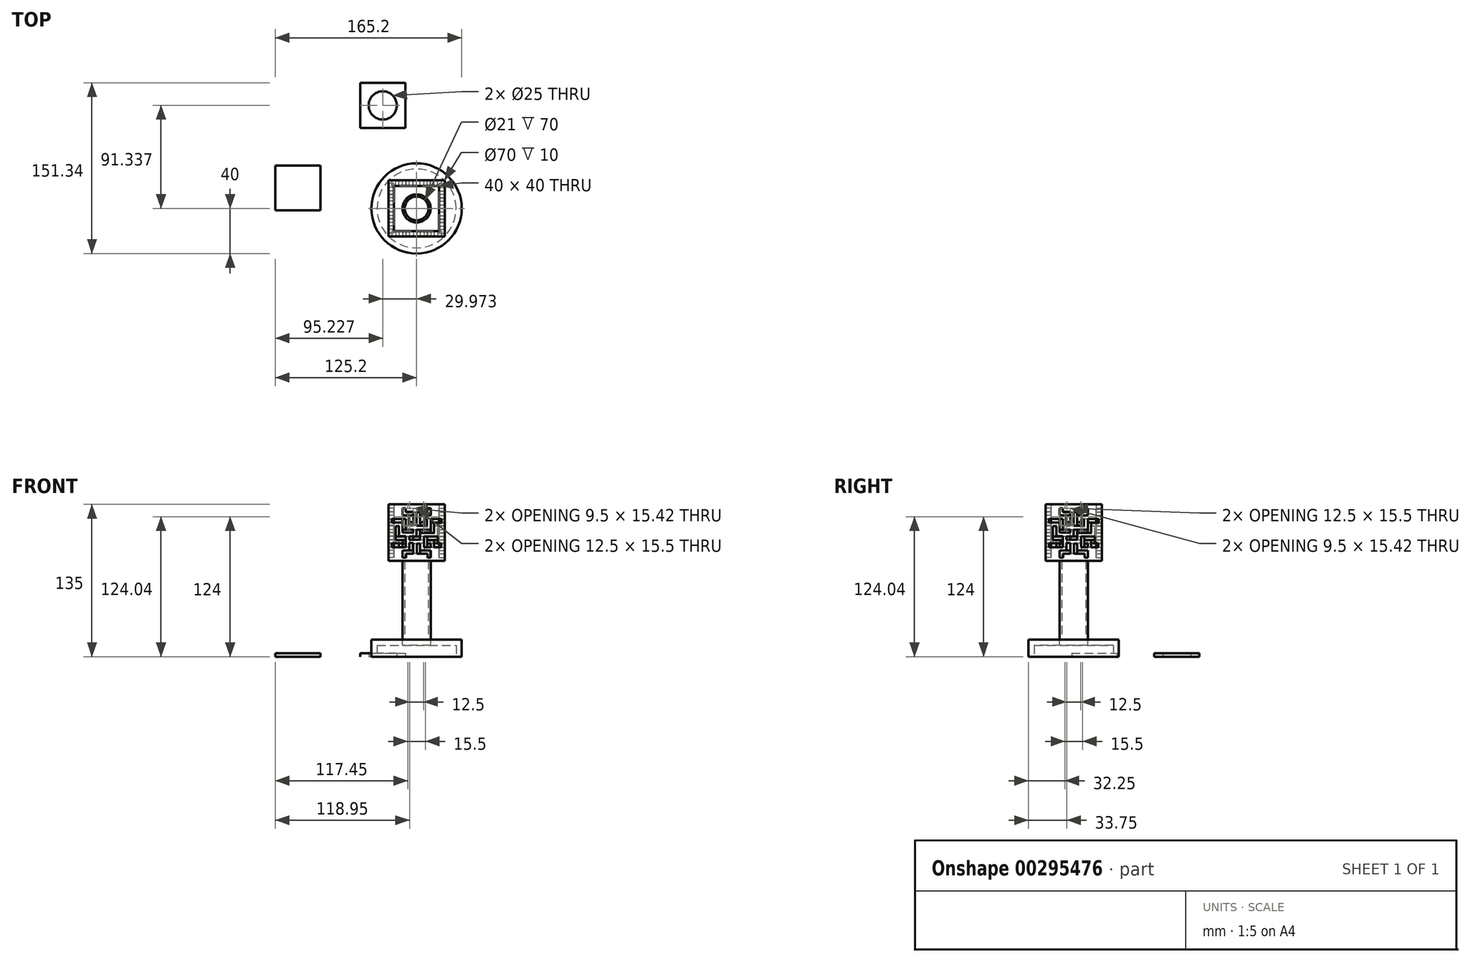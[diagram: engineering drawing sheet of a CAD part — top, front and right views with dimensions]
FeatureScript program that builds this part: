
annotation { "Feature Type Name" : "Feature", "Feature Type Description" : "" }
export const myFeature = defineFeature(function(context is Context, id is Id, definition is map)
    precondition{}
    {
        {
            var Q0;
            Q0=qCreatedBy(makeId("Top.planeOp"),FACE);
            var sketch = newSketch(context, id + "F0", { "sketchPlane" : qUnion([Q0])});
            skCircle(sketch, "E0", {"center": v(0, 0) * mm, "radius": 40 * mm});
            skSolve(sketch);
        }
        {
            var Q0;
            Q0=makeQuery(id+"F0.imprint","IMPRINT",FACE,{"disambiguationData":[TD([[makeQuery(id+"F0.imprint","IMPRINT",EDGE,{"derivedFrom":sQuery(id+"F0.wireOp",EDGE,"E0")}),1.0]])]});
            extrude(context, id + "F1", {"entities" : qUnion([Q0]), "depth" : 15 * mm});
        }
        {
            var Q0;
            Q0=makeQuery(id+"F1.opExtrude","CAP_FACE",FACE,{"disambiguationData":[OSD([sQuery(id+"F0.wireOp",EDGE,"E0")])],"isStart":false});
            var sketch = newSketch(context, id + "F2", { "sketchPlane" : qUnion([Q0])});
            skCircle(sketch, "E1", {"center": v(0, 0) * mm, "radius": 12.5 * mm});
            skCircle(sketch, "E2", {"center": v(0, 0) * mm, "radius": 10.5 * mm});
            skSolve(sketch);
        }
        {
            var Q0;
            Q0 = qSketchRegion(id + "F2", true);
            extrude(context, id + "F3", {"entities" : qUnion([Q0]), "depth" : 70 * mm});
        }
        {
            var Q0;
            Q0=makeQuery(id+"F3.opExtrude","CAP_FACE",FACE,{"disambiguationData":[OSD([sQuery(id+"F2.wireOp",EDGE,"E1"),sQuery(id+"F2.wireOp",EDGE,"E2")])],"isStart":false});
            var sketch = newSketch(context, id + "F4", { "sketchPlane" : qUnion([Q0])});
            skLineSegment(sketch, "E3.bottom", {"start": v(25, -25) * mm, "end": v(-25, -25) * mm});
            skLineSegment(sketch, "E3.top", {"start": v(25, 25) * mm, "end": v(-25, 25) * mm});
            skLineSegment(sketch, "E3.left", {"start": v(25, -25) * mm, "end": v(25, 25) * mm});
            skLineSegment(sketch, "E3.right", {"start": v(-25, -25) * mm, "end": v(-25, 25) * mm});
            skPoint(sketch, "E3.middle", {"position": v(0, 0) * mm});
            skLineSegment(sketch, "E4.bottom", {"start": v(-20, 20) * mm, "end": v(20, 20) * mm});
            skLineSegment(sketch, "E4.top", {"start": v(-20, -20) * mm, "end": v(20, -20) * mm});
            skLineSegment(sketch, "E4.left", {"start": v(-20, 20) * mm, "end": v(-20, -20) * mm});
            skLineSegment(sketch, "E4.right", {"start": v(20, 20) * mm, "end": v(20, -20) * mm});
            skSolve(sketch);
        }
        {
            var Q0;
            Q0=qCreatedBy(makeId("Top.planeOp"),FACE);
            var sketch = newSketch(context, id + "F5", { "sketchPlane" : qUnion([Q0])});
            skPoint(sketch, "E5.middle", {"position": v(-105.2, 18.16) * mm});
            skLineSegment(sketch, "E6.bottom", {"start": v(-125.2, -1.84) * mm, "end": v(-85.2, -1.84) * mm});
            skLineSegment(sketch, "E6.top", {"start": v(-125.2, 38.16) * mm, "end": v(-85.2, 38.16) * mm});
            skLineSegment(sketch, "E6.left", {"start": v(-125.2, -1.84) * mm, "end": v(-125.2, 38.16) * mm});
            skLineSegment(sketch, "E6.right", {"start": v(-85.2, -1.84) * mm, "end": v(-85.2, 38.16) * mm});
            skSolve(sketch);
        }
        {
            var Q0;
            Q0 = qSketchRegion(id + "F5", true);
            extrude(context, id + "F6", {"entities" : qUnion([Q0]), "depth" : 3 * mm});
        }
        {
            var Q0;
            Q0=qCreatedBy(makeId("Top.planeOp"),FACE);
            var sketch = newSketch(context, id + "F7", { "sketchPlane" : qUnion([Q0])});
            skPoint(sketch, "E7.middle", {"position": v(-29.97, 91.34) * mm});
            skCircle(sketch, "E8", {"center": v(-29.97, 91.34) * mm, "radius": 12.5 * mm});
            skLineSegment(sketch, "E9.bottom", {"start": v(-49.97, 71.34) * mm, "end": v(-9.97, 71.34) * mm});
            skLineSegment(sketch, "E9.top", {"start": v(-49.97, 111.34) * mm, "end": v(-9.97, 111.34) * mm});
            skLineSegment(sketch, "E9.left", {"start": v(-49.97, 71.34) * mm, "end": v(-49.97, 111.34) * mm});
            skLineSegment(sketch, "E9.right", {"start": v(-9.97, 71.34) * mm, "end": v(-9.97, 111.34) * mm});
            skSolve(sketch);
        }
        {
            var Q0;
            Q0 = qSketchRegion(id + "F7", true);
            extrude(context, id + "F8", {"entities" : qUnion([Q0]), "depth" : 3 * mm});
        }
        {
            var Q0;
            Q0 = qSketchRegion(id + "F4", true);
            extrude(context, id + "F9", {"entities" : qUnion([Q0]), "depth" : 50 * mm});
        }
        {
            var Q0;
            Q0=makeQuery(id+"F9.opExtrude","SWEPT_FACE",FACE,{"disambiguationData":[OSD([sQuery(id+"F4.wireOp",EDGE,"E3.bottom")])]});
            var sketch = newSketch(context, id + "F10", { "sketchPlane" : qUnion([Q0])});
            skLineSegment(sketch, "E10.top", {"start": v(-12.56, 125.35) * mm, "end": v(-9.48, 125.35) * mm});
            skLineSegment(sketch, "E11.left", {"start": v(-12.5, 128.35) * mm, "end": v(-12.5, 125.25) * mm});
            skLineSegment(sketch, "E11.right", {"start": v(-3, 128.33) * mm, "end": v(-3, 125.31) * mm});
            skLineSegment(sketch, "E12.top", {"start": v(-6.5, 116.33) * mm, "end": v(-3, 116.33) * mm});
            skLineSegment(sketch, "E12.left", {"start": v(-6.5, 125.33) * mm, "end": v(-6.5, 116.33) * mm});
            skLineSegment(sketch, "E12.right", {"start": v(-3, 125.31) * mm, "end": v(-3, 116.33) * mm});
            skLineSegment(sketch, "E13", {"start": v(-9.48, 125.35) * mm, "end": v(-6.5, 125.33) * mm});
            skLineSegment(sketch, "E14", {"start": v(-3, 128.33) * mm, "end": v(-9.5, 128.33) * mm});
            skLineSegment(sketch, "E15.top", {"start": v(9.5, 125.25) * mm, "end": v(12.5, 125.25) * mm});
            skLineSegment(sketch, "E16.left", {"start": v(12.5, 125.25) * mm, "end": v(12.5, 128.25) * mm});
            skLineSegment(sketch, "E16.right", {"start": v(0, 125.25) * mm, "end": v(0, 128.25) * mm});
            skLineSegment(sketch, "E17.bottom", {"start": v(0, 128.25) * mm, "end": v(3, 128.25) * mm});
            skLineSegment(sketch, "E17.top", {"start": v(0, 116.25) * mm, "end": v(3, 116.25) * mm});
            skLineSegment(sketch, "E17.left", {"start": v(0, 128.25) * mm, "end": v(0, 116.25) * mm});
            skLineSegment(sketch, "E18.bottom", {"start": v(0, 116.25) * mm, "end": v(9, 116.25) * mm});
            skLineSegment(sketch, "E18.left", {"start": v(0, 116.25) * mm, "end": v(0, 119.25) * mm});
            skLineSegment(sketch, "E18.right", {"start": v(9, 116.25) * mm, "end": v(9, 119.25) * mm});
            skLineSegment(sketch, "E19.bottom", {"start": v(9, 116.25) * mm, "end": v(6.5, 116.25) * mm});
            skLineSegment(sketch, "E19.top", {"start": v(9, 121.75) * mm, "end": v(6.5, 121.75) * mm});
            skLineSegment(sketch, "E19.left", {"start": v(9, 116.25) * mm, "end": v(9, 121.75) * mm});
            skLineSegment(sketch, "E20", {"start": v(6.5, 121.75) * mm, "end": v(6.5, 119.25) * mm});
            skLineSegment(sketch, "E21", {"start": v(3, 125.25) * mm, "end": v(3, 119.25) * mm});
            skLineSegment(sketch, "E22", {"start": v(3, 119.25) * mm, "end": v(6.5, 119.25) * mm});
            skLineSegment(sketch, "E23", {"start": v(3, 128.25) * mm, "end": v(9.5, 128.25) * mm});
            skLineSegment(sketch, "E24", {"start": v(3, 125.25) * mm, "end": v(9.5, 125.25) * mm});
            skLineSegment(sketch, "E25.right", {"start": v(-9.5, 122) * mm, "end": v(-9.5, 119) * mm});
            skLineSegment(sketch, "E26.top", {"start": v(-9.5, 110) * mm, "end": v(-12.5, 110) * mm});
            skLineSegment(sketch, "E26.right", {"start": v(-12.5, 119) * mm, "end": v(-12.5, 110) * mm});
            skLineSegment(sketch, "E27.bottom", {"start": v(-12.5, 110) * mm, "end": v(-3, 110) * mm});
            skLineSegment(sketch, "E27.left", {"start": v(-12.5, 110) * mm, "end": v(-12.5, 112.5) * mm});
            skLineSegment(sketch, "E27.right", {"start": v(-3, 110) * mm, "end": v(-3, 112.5) * mm});
            skLineSegment(sketch, "E28", {"start": v(-9.5, 119) * mm, "end": v(-9.5, 112.5) * mm});
            skLineSegment(sketch, "E29", {"start": v(-9.5, 112.5) * mm, "end": v(-3, 112.5) * mm});
            skLineSegment(sketch, "E30.right", {"start": v(-9.5, 100.41) * mm, "end": v(-9.5, 96.91) * mm});
            skLineSegment(sketch, "E31.bottom", {"start": v(-9.5, 96.91) * mm, "end": v(-12, 96.91) * mm});
            skLineSegment(sketch, "E31.top", {"start": v(-9.5, 106.91) * mm, "end": v(-12.04, 106.91) * mm});
            skLineSegment(sketch, "E31.left", {"start": v(-9.5, 96.91) * mm, "end": v(-9.5, 106.91) * mm});
            skLineSegment(sketch, "E32.left", {"start": v(-9.5, 106.91) * mm, "end": v(-9.5, 103.41) * mm});
            skLineSegment(sketch, "E32.right", {"start": v(-18.5, 106.91) * mm, "end": v(-18.5, 103.41) * mm});
            skLineSegment(sketch, "E33.bottom", {"start": v(-18.5, 103.41) * mm, "end": v(-15.5, 103.41) * mm});
            skLineSegment(sketch, "E33.top", {"start": v(-18.5, 115.91) * mm, "end": v(-15.54, 115.91) * mm});
            skLineSegment(sketch, "E33.left", {"start": v(-18.5, 103.41) * mm, "end": v(-18.5, 115.91) * mm});
            skLineSegment(sketch, "E34", {"start": v(-12.04, 100.41) * mm, "end": v(-12.04, 103.41) * mm});
            skLineSegment(sketch, "E35", {"start": v(-15.54, 115.91) * mm, "end": v(-15.54, 106.91) * mm});
            skLineSegment(sketch, "E36", {"start": v(-12.04, 106.91) * mm, "end": v(-15.54, 106.91) * mm});
            skLineSegment(sketch, "E37", {"start": v(-12.04, 103.41) * mm, "end": v(-15.5, 103.41) * mm});
            skLineSegment(sketch, "E38.top", {"start": v(-12.4, 94.25) * mm, "end": v(-9.44, 94.25) * mm});
            skLineSegment(sketch, "E39.left", {"start": v(-12.4, 94.25) * mm, "end": v(-12.4, 91.25) * mm});
            skLineSegment(sketch, "E39.right", {"start": v(-2.94, 94.25) * mm, "end": v(-2.94, 91.25) * mm});
            skLineSegment(sketch, "E40.bottom", {"start": v(-2.94, 91.25) * mm, "end": v(-6.4, 91.25) * mm});
            skLineSegment(sketch, "E40.top", {"start": v(-2.94, 100.75) * mm, "end": v(-6.44, 100.75) * mm});
            skLineSegment(sketch, "E40.left", {"start": v(-2.94, 91.25) * mm, "end": v(-2.94, 100.75) * mm});
            skLineSegment(sketch, "E41", {"start": v(-6.4, 91.25) * mm, "end": v(-9.4, 91.25) * mm});
            skLineSegment(sketch, "E42", {"start": v(-6.44, 100.75) * mm, "end": v(-6.44, 94.25) * mm});
            skLineSegment(sketch, "E43", {"start": v(-9.44, 94.25) * mm, "end": v(-6.44, 94.25) * mm});
            skLineSegment(sketch, "E44.top", {"start": v(12.61, 94.25) * mm, "end": v(9.61, 94.25) * mm});
            skLineSegment(sketch, "E45.left", {"start": v(12.61, 94.25) * mm, "end": v(12.61, 91.25) * mm});
            skLineSegment(sketch, "E45.right", {"start": v(0.11, 94.25) * mm, "end": v(0.11, 91.25) * mm});
            skLineSegment(sketch, "E46.bottom", {"start": v(0.11, 91.25) * mm, "end": v(3.11, 91.25) * mm});
            skLineSegment(sketch, "E46.top", {"start": v(0.11, 100.25) * mm, "end": v(3.11, 100.25) * mm});
            skLineSegment(sketch, "E46.left", {"start": v(0.11, 91.25) * mm, "end": v(0.11, 100.25) * mm});
            skLineSegment(sketch, "E47", {"start": v(3.11, 100.25) * mm, "end": v(3.11, 94.25) * mm});
            skLineSegment(sketch, "E48", {"start": v(9.61, 94.25) * mm, "end": v(3.11, 94.25) * mm});
            skLineSegment(sketch, "E49", {"start": v(3.11, 91.25) * mm, "end": v(9.61, 91.25) * mm});
            skLineSegment(sketch, "E50.right", {"start": v(15.5, 97.17) * mm, "end": v(15.5, 100.67) * mm});
            skLineSegment(sketch, "E51.bottom", {"start": v(15.5, 97.17) * mm, "end": v(18.5, 97.17) * mm});
            skLineSegment(sketch, "E51.top", {"start": v(15.5, 106.67) * mm, "end": v(18.5, 106.67) * mm});
            skLineSegment(sketch, "E52.bottom", {"start": v(18.5, 106.67) * mm, "end": v(6.5, 106.67) * mm});
            skLineSegment(sketch, "E52.left", {"start": v(18.5, 106.67) * mm, "end": v(18.5, 103.17) * mm});
            skLineSegment(sketch, "E52.right", {"start": v(6.5, 106.67) * mm, "end": v(6.5, 103.17) * mm});
            skLineSegment(sketch, "E53.bottom", {"start": v(6.5, 106.67) * mm, "end": v(9.5, 106.67) * mm});
            skLineSegment(sketch, "E53.top", {"start": v(6.5, 97.17) * mm, "end": v(9.5, 97.17) * mm});
            skLineSegment(sketch, "E53.left", {"start": v(6.5, 106.67) * mm, "end": v(6.5, 97.17) * mm});
            skLineSegment(sketch, "E54.bottom", {"start": v(6.5, 97.17) * mm, "end": v(12.5, 97.17) * mm});
            skLineSegment(sketch, "E54.left", {"start": v(6.5, 97.17) * mm, "end": v(6.5, 100.17) * mm});
            skLineSegment(sketch, "E54.right", {"start": v(12.5, 97.17) * mm, "end": v(12.5, 100.17) * mm});
            skLineSegment(sketch, "E55.right", {"start": v(12.5, 122.17) * mm, "end": v(12.5, 118.67) * mm});
            skLineSegment(sketch, "E56.bottom", {"start": v(12.5, 122.17) * mm, "end": v(15.5, 122.17) * mm});
            skLineSegment(sketch, "E56.top", {"start": v(12.5, 109.67) * mm, "end": v(15.5, 109.67) * mm});
            skPoint(sketch, "E57.oppositeSnap0", {"position": v(0, 117.75) * mm});
            skLineSegment(sketch, "E57.left", {"start": v(15.5, 109.67) * mm, "end": v(15.5, 112.67) * mm});
            skLineSegment(sketch, "E57.right", {"start": v(0, 109.67) * mm, "end": v(0, 112.67) * mm});
            skLineSegment(sketch, "E58.bottom", {"start": v(0, 112.67) * mm, "end": v(3, 112.67) * mm});
            skLineSegment(sketch, "E58.top", {"start": v(0, 103.67) * mm, "end": v(3, 103.67) * mm});
            skLineSegment(sketch, "E59.bottom", {"start": v(3, 103.67) * mm, "end": v(-6.5, 103.67) * mm});
            skLineSegment(sketch, "E59.left", {"start": v(3, 103.67) * mm, "end": v(3, 106.67) * mm});
            skLineSegment(sketch, "E59.right", {"start": v(-6.5, 103.67) * mm, "end": v(-6.5, 106.67) * mm});
            skLineSegment(sketch, "E60", {"start": v(15.5, 112.67) * mm, "end": v(15.5, 118.67) * mm});
            skLineSegment(sketch, "E61", {"start": v(3, 112.67) * mm, "end": v(12.5, 112.67) * mm});
            skLineSegment(sketch, "E62", {"start": v(12.5, 112.67) * mm, "end": v(12.5, 122.17) * mm});
            skLineSegment(sketch, "E63", {"start": v(3, 106.67) * mm, "end": v(3, 109.67) * mm});
            skLineSegment(sketch, "E64", {"start": v(-6.5, 106.67) * mm, "end": v(0, 106.67) * mm});
            skLineSegment(sketch, "E65", {"start": v(0, 106.67) * mm, "end": v(0, 109.67) * mm});
            skLineSegment(sketch, "E66", {"start": v(3, 109.67) * mm, "end": v(12.5, 109.67) * mm});
            skLineSegment(sketch, "E67", {"start": v(18.5, 103.17) * mm, "end": v(18.5, 100.67) * mm});
            skLineSegment(sketch, "E68", {"start": v(9.5, 103.4) * mm, "end": v(15.5, 103.4) * mm});
            skLineSegment(sketch, "E69", {"start": v(15.5, 100.67) * mm, "end": v(15.5, 103.4) * mm});
            skLineSegment(sketch, "E70", {"start": v(9.5, 103.4) * mm, "end": v(9.5, 100.17) * mm});
            skLineSegment(sketch, "E71", {"start": v(9.5, 100.17) * mm, "end": v(12.5, 100.17) * mm});
            skLineSegment(sketch, "E72.right", {"start": v(-22, 122) * mm, "end": v(-22, 119) * mm});
            skLineSegment(sketch, "E73", {"start": v(-22, 119) * mm, "end": v(-12.5, 119) * mm});
            skLineSegment(sketch, "E74", {"start": v(-22, 122) * mm, "end": v(-9.5, 122) * mm});
            skLineSegment(sketch, "E75.right", {"start": v(-22, 100.41) * mm, "end": v(-22, 96.91) * mm});
            skLineSegment(sketch, "E76", {"start": v(-12, 96.91) * mm, "end": v(-22, 96.91) * mm});
            skLineSegment(sketch, "E77", {"start": v(-22, 100.41) * mm, "end": v(-12.04, 100.41) * mm});
            skLineSegment(sketch, "E78.top", {"start": v(-12.4, 88) * mm, "end": v(-9.4, 88) * mm});
            skLineSegment(sketch, "E79", {"start": v(-9.4, 88) * mm, "end": v(-9.4, 91.25) * mm});
            skLineSegment(sketch, "E80", {"start": v(-12.4, 88) * mm, "end": v(-12.4, 91.25) * mm});
            skLineSegment(sketch, "E81.top", {"start": v(9.61, 87.75) * mm, "end": v(12.61, 87.75) * mm});
            skLineSegment(sketch, "E82", {"start": v(9.61, 87.75) * mm, "end": v(9.61, 91.25) * mm});
            skLineSegment(sketch, "E83", {"start": v(12.61, 87.75) * mm, "end": v(12.61, 91.25) * mm});
            skLineSegment(sketch, "E84.right", {"start": v(21.75, 97.17) * mm, "end": v(21.75, 100.67) * mm});
            skLineSegment(sketch, "E85", {"start": v(21.75, 97.17) * mm, "end": v(18.5, 97.17) * mm});
            skLineSegment(sketch, "E86", {"start": v(21.75, 100.67) * mm, "end": v(18.5, 100.67) * mm});
            skLineSegment(sketch, "E87.right", {"start": v(22, 118.67) * mm, "end": v(22, 122.17) * mm});
            skLineSegment(sketch, "E88", {"start": v(22, 118.67) * mm, "end": v(15.5, 118.67) * mm});
            skLineSegment(sketch, "E89", {"start": v(22, 122.17) * mm, "end": v(15.5, 122.17) * mm});
            skLineSegment(sketch, "E90.top", {"start": v(9.5, 131.75) * mm, "end": v(12.5, 131.75) * mm});
            skLineSegment(sketch, "E91", {"start": v(9.5, 131.75) * mm, "end": v(9.5, 128.25) * mm});
            skLineSegment(sketch, "E92", {"start": v(12.5, 131.75) * mm, "end": v(12.5, 128.25) * mm});
            skLineSegment(sketch, "E93.top", {"start": v(-12.5, 131.75) * mm, "end": v(-9.5, 131.75) * mm});
            skLineSegment(sketch, "E94", {"start": v(-12.5, 131.75) * mm, "end": v(-12.5, 128.35) * mm});
            skLineSegment(sketch, "E95", {"start": v(-9.5, 131.75) * mm, "end": v(-9.5, 128.33) * mm});
            skSolve(sketch);
        }
        {
            var Q0;
            Q0=makeQuery(id+"F9.opExtrude","SWEPT_FACE",FACE,{"disambiguationData":[OSD([sQuery(id+"F4.wireOp",EDGE,"E3.left")])]});
            var sketch = newSketch(context, id + "F11", { "sketchPlane" : qUnion([Q0])});
            skLineSegment(sketch, "E96.top", {"start": v(-12.56, 125.35) * mm, "end": v(-9.48, 125.35) * mm});
            skLineSegment(sketch, "E97.left", {"start": v(-12.5, 128.35) * mm, "end": v(-12.5, 125.25) * mm});
            skLineSegment(sketch, "E97.right", {"start": v(-3, 128.33) * mm, "end": v(-3, 125.31) * mm});
            skLineSegment(sketch, "E98.top", {"start": v(-6.5, 116.33) * mm, "end": v(-3, 116.33) * mm});
            skLineSegment(sketch, "E98.left", {"start": v(-6.5, 125.33) * mm, "end": v(-6.5, 116.33) * mm});
            skLineSegment(sketch, "E98.right", {"start": v(-3, 125.31) * mm, "end": v(-3, 116.33) * mm});
            skLineSegment(sketch, "E99", {"start": v(-9.48, 125.35) * mm, "end": v(-6.5, 125.33) * mm});
            skLineSegment(sketch, "E100", {"start": v(-3, 128.33) * mm, "end": v(-9.5, 128.33) * mm});
            skLineSegment(sketch, "E101.top", {"start": v(9.5, 125.25) * mm, "end": v(12.5, 125.25) * mm});
            skLineSegment(sketch, "E102.left", {"start": v(12.5, 125.25) * mm, "end": v(12.5, 128.25) * mm});
            skLineSegment(sketch, "E102.right", {"start": v(0, 125.25) * mm, "end": v(0, 128.25) * mm});
            skLineSegment(sketch, "E103.bottom", {"start": v(0, 128.25) * mm, "end": v(3, 128.25) * mm});
            skLineSegment(sketch, "E103.top", {"start": v(0, 116.25) * mm, "end": v(3, 116.25) * mm});
            skLineSegment(sketch, "E103.left", {"start": v(0, 128.25) * mm, "end": v(0, 116.25) * mm});
            skLineSegment(sketch, "E104.bottom", {"start": v(0, 116.25) * mm, "end": v(9, 116.25) * mm});
            skLineSegment(sketch, "E104.left", {"start": v(0, 116.25) * mm, "end": v(0, 119.25) * mm});
            skLineSegment(sketch, "E104.right", {"start": v(9, 116.25) * mm, "end": v(9, 119.25) * mm});
            skLineSegment(sketch, "E105.bottom", {"start": v(9, 116.25) * mm, "end": v(6.5, 116.25) * mm});
            skLineSegment(sketch, "E105.top", {"start": v(9, 121.75) * mm, "end": v(6.5, 121.75) * mm});
            skLineSegment(sketch, "E105.left", {"start": v(9, 116.25) * mm, "end": v(9, 121.75) * mm});
            skLineSegment(sketch, "E106", {"start": v(6.5, 121.75) * mm, "end": v(6.5, 119.25) * mm});
            skLineSegment(sketch, "E107", {"start": v(3, 125.25) * mm, "end": v(3, 119.25) * mm});
            skLineSegment(sketch, "E108", {"start": v(3, 119.25) * mm, "end": v(6.5, 119.25) * mm});
            skLineSegment(sketch, "E109", {"start": v(3, 128.25) * mm, "end": v(9.5, 128.25) * mm});
            skLineSegment(sketch, "E110", {"start": v(3, 125.25) * mm, "end": v(9.5, 125.25) * mm});
            skLineSegment(sketch, "E111.right", {"start": v(-9.5, 122) * mm, "end": v(-9.5, 119) * mm});
            skLineSegment(sketch, "E112.top", {"start": v(-9.5, 110) * mm, "end": v(-12.5, 110) * mm});
            skLineSegment(sketch, "E112.right", {"start": v(-12.5, 119) * mm, "end": v(-12.5, 110) * mm});
            skLineSegment(sketch, "E113.bottom", {"start": v(-12.5, 110) * mm, "end": v(-3, 110) * mm});
            skLineSegment(sketch, "E113.left", {"start": v(-12.5, 110) * mm, "end": v(-12.5, 112.5) * mm});
            skLineSegment(sketch, "E113.right", {"start": v(-3, 110) * mm, "end": v(-3, 112.5) * mm});
            skLineSegment(sketch, "E114", {"start": v(-9.5, 119) * mm, "end": v(-9.5, 112.5) * mm});
            skLineSegment(sketch, "E115", {"start": v(-9.5, 112.5) * mm, "end": v(-3, 112.5) * mm});
            skLineSegment(sketch, "E116.right", {"start": v(-9.5, 100.41) * mm, "end": v(-9.5, 96.91) * mm});
            skLineSegment(sketch, "E117.bottom", {"start": v(-9.5, 96.91) * mm, "end": v(-12, 96.91) * mm});
            skLineSegment(sketch, "E117.top", {"start": v(-9.5, 106.91) * mm, "end": v(-12.04, 106.91) * mm});
            skLineSegment(sketch, "E117.left", {"start": v(-9.5, 96.91) * mm, "end": v(-9.5, 106.91) * mm});
            skLineSegment(sketch, "E118.left", {"start": v(-9.5, 106.91) * mm, "end": v(-9.5, 103.41) * mm});
            skLineSegment(sketch, "E118.right", {"start": v(-18.5, 106.91) * mm, "end": v(-18.5, 103.41) * mm});
            skLineSegment(sketch, "E119.bottom", {"start": v(-18.5, 103.41) * mm, "end": v(-15.5, 103.41) * mm});
            skLineSegment(sketch, "E119.top", {"start": v(-18.5, 115.91) * mm, "end": v(-15.54, 115.91) * mm});
            skLineSegment(sketch, "E119.left", {"start": v(-18.5, 103.41) * mm, "end": v(-18.5, 115.91) * mm});
            skLineSegment(sketch, "E120", {"start": v(-12.04, 100.41) * mm, "end": v(-12.04, 103.41) * mm});
            skLineSegment(sketch, "E121", {"start": v(-15.54, 115.91) * mm, "end": v(-15.54, 106.91) * mm});
            skLineSegment(sketch, "E122", {"start": v(-12.04, 106.91) * mm, "end": v(-15.54, 106.91) * mm});
            skLineSegment(sketch, "E123", {"start": v(-12.04, 103.41) * mm, "end": v(-15.5, 103.41) * mm});
            skLineSegment(sketch, "E124.top", {"start": v(-12.4, 94.25) * mm, "end": v(-9.44, 94.25) * mm});
            skLineSegment(sketch, "E125.left", {"start": v(-12.4, 94.25) * mm, "end": v(-12.4, 91.25) * mm});
            skLineSegment(sketch, "E125.right", {"start": v(-2.94, 94.25) * mm, "end": v(-2.94, 91.25) * mm});
            skLineSegment(sketch, "E126.bottom", {"start": v(-2.94, 91.25) * mm, "end": v(-6.4, 91.25) * mm});
            skLineSegment(sketch, "E126.top", {"start": v(-2.94, 100.75) * mm, "end": v(-6.44, 100.75) * mm});
            skLineSegment(sketch, "E126.left", {"start": v(-2.94, 91.25) * mm, "end": v(-2.94, 100.75) * mm});
            skLineSegment(sketch, "E127", {"start": v(-6.4, 91.25) * mm, "end": v(-9.4, 91.25) * mm});
            skLineSegment(sketch, "E128", {"start": v(-6.44, 100.75) * mm, "end": v(-6.44, 94.25) * mm});
            skLineSegment(sketch, "E129", {"start": v(-9.44, 94.25) * mm, "end": v(-6.44, 94.25) * mm});
            skLineSegment(sketch, "E130.top", {"start": v(12.61, 94.25) * mm, "end": v(9.61, 94.25) * mm});
            skLineSegment(sketch, "E131.left", {"start": v(12.61, 94.25) * mm, "end": v(12.61, 91.25) * mm});
            skLineSegment(sketch, "E131.right", {"start": v(0.11, 94.25) * mm, "end": v(0.11, 91.25) * mm});
            skLineSegment(sketch, "E132.bottom", {"start": v(0.11, 91.25) * mm, "end": v(3.11, 91.25) * mm});
            skLineSegment(sketch, "E132.top", {"start": v(0.11, 100.25) * mm, "end": v(3.11, 100.25) * mm});
            skLineSegment(sketch, "E132.left", {"start": v(0.11, 91.25) * mm, "end": v(0.11, 100.25) * mm});
            skLineSegment(sketch, "E133", {"start": v(3.11, 100.25) * mm, "end": v(3.11, 94.25) * mm});
            skLineSegment(sketch, "E134", {"start": v(9.61, 94.25) * mm, "end": v(3.11, 94.25) * mm});
            skLineSegment(sketch, "E135", {"start": v(3.11, 91.25) * mm, "end": v(9.61, 91.25) * mm});
            skLineSegment(sketch, "E136.right", {"start": v(15.5, 97.17) * mm, "end": v(15.5, 100.67) * mm});
            skLineSegment(sketch, "E137.bottom", {"start": v(15.5, 97.17) * mm, "end": v(18.5, 97.17) * mm});
            skLineSegment(sketch, "E137.top", {"start": v(15.5, 106.67) * mm, "end": v(18.5, 106.67) * mm});
            skLineSegment(sketch, "E138.bottom", {"start": v(18.5, 106.67) * mm, "end": v(6.5, 106.67) * mm});
            skLineSegment(sketch, "E138.left", {"start": v(18.5, 106.67) * mm, "end": v(18.5, 103.17) * mm});
            skLineSegment(sketch, "E138.right", {"start": v(6.5, 106.67) * mm, "end": v(6.5, 103.17) * mm});
            skLineSegment(sketch, "E139.bottom", {"start": v(6.5, 106.67) * mm, "end": v(9.5, 106.67) * mm});
            skLineSegment(sketch, "E139.top", {"start": v(6.5, 97.17) * mm, "end": v(9.5, 97.17) * mm});
            skLineSegment(sketch, "E139.left", {"start": v(6.5, 106.67) * mm, "end": v(6.5, 97.17) * mm});
            skLineSegment(sketch, "E140.bottom", {"start": v(6.5, 97.17) * mm, "end": v(12.5, 97.17) * mm});
            skLineSegment(sketch, "E140.left", {"start": v(6.5, 97.17) * mm, "end": v(6.5, 100.17) * mm});
            skLineSegment(sketch, "E140.right", {"start": v(12.5, 97.17) * mm, "end": v(12.5, 100.17) * mm});
            skLineSegment(sketch, "E141.right", {"start": v(12.5, 122.17) * mm, "end": v(12.5, 118.67) * mm});
            skLineSegment(sketch, "E142.bottom", {"start": v(12.5, 122.17) * mm, "end": v(15.5, 122.17) * mm});
            skLineSegment(sketch, "E142.top", {"start": v(12.5, 109.67) * mm, "end": v(15.5, 109.67) * mm});
            skPoint(sketch, "E143.oppositeSnap0", {"position": v(0, 117.75) * mm});
            skLineSegment(sketch, "E143.left", {"start": v(15.5, 109.67) * mm, "end": v(15.5, 112.67) * mm});
            skLineSegment(sketch, "E143.right", {"start": v(0, 109.67) * mm, "end": v(0, 112.67) * mm});
            skLineSegment(sketch, "E144.bottom", {"start": v(0, 112.67) * mm, "end": v(3, 112.67) * mm});
            skLineSegment(sketch, "E144.top", {"start": v(0, 103.67) * mm, "end": v(3, 103.67) * mm});
            skLineSegment(sketch, "E145.bottom", {"start": v(3, 103.67) * mm, "end": v(-6.5, 103.67) * mm});
            skLineSegment(sketch, "E145.left", {"start": v(3, 103.67) * mm, "end": v(3, 106.67) * mm});
            skLineSegment(sketch, "E145.right", {"start": v(-6.5, 103.67) * mm, "end": v(-6.5, 106.67) * mm});
            skLineSegment(sketch, "E146", {"start": v(15.5, 112.67) * mm, "end": v(15.5, 118.67) * mm});
            skLineSegment(sketch, "E147", {"start": v(3, 112.67) * mm, "end": v(12.5, 112.67) * mm});
            skLineSegment(sketch, "E148", {"start": v(12.5, 112.67) * mm, "end": v(12.5, 122.17) * mm});
            skLineSegment(sketch, "E149", {"start": v(3, 106.67) * mm, "end": v(3, 109.67) * mm});
            skLineSegment(sketch, "E150", {"start": v(-6.5, 106.67) * mm, "end": v(0, 106.67) * mm});
            skLineSegment(sketch, "E151", {"start": v(0, 106.67) * mm, "end": v(0, 109.67) * mm});
            skLineSegment(sketch, "E152", {"start": v(3, 109.67) * mm, "end": v(12.5, 109.67) * mm});
            skLineSegment(sketch, "E153", {"start": v(18.5, 103.17) * mm, "end": v(18.5, 100.67) * mm});
            skLineSegment(sketch, "E154", {"start": v(9.5, 103.4) * mm, "end": v(15.5, 103.4) * mm});
            skLineSegment(sketch, "E155", {"start": v(15.5, 100.67) * mm, "end": v(15.5, 103.4) * mm});
            skLineSegment(sketch, "E156", {"start": v(9.5, 103.4) * mm, "end": v(9.5, 100.17) * mm});
            skLineSegment(sketch, "E157", {"start": v(9.5, 100.17) * mm, "end": v(12.5, 100.17) * mm});
            skLineSegment(sketch, "E158.right", {"start": v(-22, 122) * mm, "end": v(-22, 119) * mm});
            skLineSegment(sketch, "E159", {"start": v(-22, 119) * mm, "end": v(-12.5, 119) * mm});
            skLineSegment(sketch, "E160", {"start": v(-22, 122) * mm, "end": v(-9.5, 122) * mm});
            skLineSegment(sketch, "E161.right", {"start": v(-22, 100.41) * mm, "end": v(-22, 96.91) * mm});
            skLineSegment(sketch, "E162", {"start": v(-12, 96.91) * mm, "end": v(-22, 96.91) * mm});
            skLineSegment(sketch, "E163", {"start": v(-22, 100.41) * mm, "end": v(-12.04, 100.41) * mm});
            skLineSegment(sketch, "E164.top", {"start": v(-12.4, 88) * mm, "end": v(-9.4, 88) * mm});
            skLineSegment(sketch, "E165", {"start": v(-9.4, 88) * mm, "end": v(-9.4, 91.25) * mm});
            skLineSegment(sketch, "E166", {"start": v(-12.4, 88) * mm, "end": v(-12.4, 91.25) * mm});
            skLineSegment(sketch, "E167.top", {"start": v(9.61, 87.75) * mm, "end": v(12.61, 87.75) * mm});
            skLineSegment(sketch, "E168", {"start": v(9.61, 87.75) * mm, "end": v(9.61, 91.25) * mm});
            skLineSegment(sketch, "E169", {"start": v(12.61, 87.75) * mm, "end": v(12.61, 91.25) * mm});
            skLineSegment(sketch, "E170.right", {"start": v(21.75, 97.17) * mm, "end": v(21.75, 100.67) * mm});
            skLineSegment(sketch, "E171", {"start": v(21.75, 97.17) * mm, "end": v(18.5, 97.17) * mm});
            skLineSegment(sketch, "E172", {"start": v(21.75, 100.67) * mm, "end": v(18.5, 100.67) * mm});
            skLineSegment(sketch, "E173.right", {"start": v(22, 118.67) * mm, "end": v(22, 122.17) * mm});
            skLineSegment(sketch, "E174", {"start": v(22, 118.67) * mm, "end": v(15.5, 118.67) * mm});
            skLineSegment(sketch, "E175", {"start": v(22, 122.17) * mm, "end": v(15.5, 122.17) * mm});
            skLineSegment(sketch, "E176.top", {"start": v(9.5, 131.75) * mm, "end": v(12.5, 131.75) * mm});
            skLineSegment(sketch, "E177", {"start": v(9.5, 131.75) * mm, "end": v(9.5, 128.25) * mm});
            skLineSegment(sketch, "E178", {"start": v(12.5, 131.75) * mm, "end": v(12.5, 128.25) * mm});
            skLineSegment(sketch, "E179.top", {"start": v(-12.5, 131.75) * mm, "end": v(-9.5, 131.75) * mm});
            skLineSegment(sketch, "E180", {"start": v(-12.5, 131.75) * mm, "end": v(-12.5, 128.35) * mm});
            skLineSegment(sketch, "E181", {"start": v(-9.5, 131.75) * mm, "end": v(-9.5, 128.33) * mm});
            skSolve(sketch);
        }
        {
            var Q0;
            Q0=makeQuery(id+"F9.opExtrude","SWEPT_FACE",FACE,{"disambiguationData":[OSD([sQuery(id+"F4.wireOp",EDGE,"E3.top")])]});
            var sketch = newSketch(context, id + "F12", { "sketchPlane" : qUnion([Q0])});
            skLineSegment(sketch, "E182.top", {"start": v(-12.56, 125.35) * mm, "end": v(-9.48, 125.35) * mm});
            skLineSegment(sketch, "E183.left", {"start": v(-12.5, 128.35) * mm, "end": v(-12.5, 125.25) * mm});
            skLineSegment(sketch, "E183.right", {"start": v(-3, 128.33) * mm, "end": v(-3, 125.31) * mm});
            skLineSegment(sketch, "E184.top", {"start": v(-6.5, 116.33) * mm, "end": v(-3, 116.33) * mm});
            skLineSegment(sketch, "E184.left", {"start": v(-6.5, 125.33) * mm, "end": v(-6.5, 116.33) * mm});
            skLineSegment(sketch, "E184.right", {"start": v(-3, 125.31) * mm, "end": v(-3, 116.33) * mm});
            skLineSegment(sketch, "E185", {"start": v(-9.48, 125.35) * mm, "end": v(-6.5, 125.33) * mm});
            skLineSegment(sketch, "E186", {"start": v(-3, 128.33) * mm, "end": v(-9.5, 128.33) * mm});
            skLineSegment(sketch, "E187.top", {"start": v(9.5, 125.25) * mm, "end": v(12.5, 125.25) * mm});
            skLineSegment(sketch, "E188.left", {"start": v(12.5, 125.25) * mm, "end": v(12.5, 128.25) * mm});
            skLineSegment(sketch, "E188.right", {"start": v(0, 125.25) * mm, "end": v(0, 128.25) * mm});
            skLineSegment(sketch, "E189.bottom", {"start": v(0, 128.25) * mm, "end": v(3, 128.25) * mm});
            skLineSegment(sketch, "E189.top", {"start": v(0, 116.25) * mm, "end": v(3, 116.25) * mm});
            skLineSegment(sketch, "E189.left", {"start": v(0, 128.25) * mm, "end": v(0, 116.25) * mm});
            skLineSegment(sketch, "E190.bottom", {"start": v(0, 116.25) * mm, "end": v(9, 116.25) * mm});
            skLineSegment(sketch, "E190.left", {"start": v(0, 116.25) * mm, "end": v(0, 119.25) * mm});
            skLineSegment(sketch, "E190.right", {"start": v(9, 116.25) * mm, "end": v(9, 119.25) * mm});
            skLineSegment(sketch, "E191.bottom", {"start": v(9, 116.25) * mm, "end": v(6.5, 116.25) * mm});
            skLineSegment(sketch, "E191.top", {"start": v(9, 121.75) * mm, "end": v(6.5, 121.75) * mm});
            skLineSegment(sketch, "E191.left", {"start": v(9, 116.25) * mm, "end": v(9, 121.75) * mm});
            skLineSegment(sketch, "E192", {"start": v(6.5, 121.75) * mm, "end": v(6.5, 119.25) * mm});
            skLineSegment(sketch, "E193", {"start": v(3, 125.25) * mm, "end": v(3, 119.25) * mm});
            skLineSegment(sketch, "E194", {"start": v(3, 119.25) * mm, "end": v(6.5, 119.25) * mm});
            skLineSegment(sketch, "E195", {"start": v(3, 128.25) * mm, "end": v(9.5, 128.25) * mm});
            skLineSegment(sketch, "E196", {"start": v(3, 125.25) * mm, "end": v(9.5, 125.25) * mm});
            skLineSegment(sketch, "E197.right", {"start": v(-9.5, 122) * mm, "end": v(-9.5, 119) * mm});
            skLineSegment(sketch, "E198.top", {"start": v(-9.5, 110) * mm, "end": v(-12.5, 110) * mm});
            skLineSegment(sketch, "E198.right", {"start": v(-12.5, 119) * mm, "end": v(-12.5, 110) * mm});
            skLineSegment(sketch, "E199.bottom", {"start": v(-12.5, 110) * mm, "end": v(-3, 110) * mm});
            skLineSegment(sketch, "E199.left", {"start": v(-12.5, 110) * mm, "end": v(-12.5, 112.5) * mm});
            skLineSegment(sketch, "E199.right", {"start": v(-3, 110) * mm, "end": v(-3, 112.5) * mm});
            skLineSegment(sketch, "E200", {"start": v(-9.5, 119) * mm, "end": v(-9.5, 112.5) * mm});
            skLineSegment(sketch, "E201", {"start": v(-9.5, 112.5) * mm, "end": v(-3, 112.5) * mm});
            skLineSegment(sketch, "E202.right", {"start": v(-9.5, 100.41) * mm, "end": v(-9.5, 96.91) * mm});
            skLineSegment(sketch, "E203.bottom", {"start": v(-9.5, 96.91) * mm, "end": v(-12, 96.91) * mm});
            skLineSegment(sketch, "E203.top", {"start": v(-9.5, 106.91) * mm, "end": v(-12.04, 106.91) * mm});
            skLineSegment(sketch, "E203.left", {"start": v(-9.5, 96.91) * mm, "end": v(-9.5, 106.91) * mm});
            skLineSegment(sketch, "E204.left", {"start": v(-9.5, 106.91) * mm, "end": v(-9.5, 103.41) * mm});
            skLineSegment(sketch, "E204.right", {"start": v(-18.5, 106.91) * mm, "end": v(-18.5, 103.41) * mm});
            skLineSegment(sketch, "E205.bottom", {"start": v(-18.5, 103.41) * mm, "end": v(-15.5, 103.41) * mm});
            skLineSegment(sketch, "E205.top", {"start": v(-18.5, 115.91) * mm, "end": v(-15.54, 115.91) * mm});
            skLineSegment(sketch, "E205.left", {"start": v(-18.5, 103.41) * mm, "end": v(-18.5, 115.91) * mm});
            skLineSegment(sketch, "E206", {"start": v(-12.04, 100.41) * mm, "end": v(-12.04, 103.41) * mm});
            skLineSegment(sketch, "E207", {"start": v(-15.54, 115.91) * mm, "end": v(-15.54, 106.91) * mm});
            skLineSegment(sketch, "E208", {"start": v(-12.04, 106.91) * mm, "end": v(-15.54, 106.91) * mm});
            skLineSegment(sketch, "E209", {"start": v(-12.04, 103.41) * mm, "end": v(-15.5, 103.41) * mm});
            skLineSegment(sketch, "E210.top", {"start": v(-12.4, 94.25) * mm, "end": v(-9.44, 94.25) * mm});
            skLineSegment(sketch, "E211.left", {"start": v(-12.4, 94.25) * mm, "end": v(-12.4, 91.25) * mm});
            skLineSegment(sketch, "E211.right", {"start": v(-2.94, 94.25) * mm, "end": v(-2.94, 91.25) * mm});
            skLineSegment(sketch, "E212.bottom", {"start": v(-2.94, 91.25) * mm, "end": v(-6.4, 91.25) * mm});
            skLineSegment(sketch, "E212.top", {"start": v(-2.94, 100.75) * mm, "end": v(-6.44, 100.75) * mm});
            skLineSegment(sketch, "E212.left", {"start": v(-2.94, 91.25) * mm, "end": v(-2.94, 100.75) * mm});
            skLineSegment(sketch, "E213", {"start": v(-6.4, 91.25) * mm, "end": v(-9.4, 91.25) * mm});
            skLineSegment(sketch, "E214", {"start": v(-6.44, 100.75) * mm, "end": v(-6.44, 94.25) * mm});
            skLineSegment(sketch, "E215", {"start": v(-9.44, 94.25) * mm, "end": v(-6.44, 94.25) * mm});
            skLineSegment(sketch, "E216.top", {"start": v(12.61, 94.25) * mm, "end": v(9.61, 94.25) * mm});
            skLineSegment(sketch, "E217.left", {"start": v(12.61, 94.25) * mm, "end": v(12.61, 91.25) * mm});
            skLineSegment(sketch, "E217.right", {"start": v(0.11, 94.25) * mm, "end": v(0.11, 91.25) * mm});
            skLineSegment(sketch, "E218.bottom", {"start": v(0.11, 91.25) * mm, "end": v(3.11, 91.25) * mm});
            skLineSegment(sketch, "E218.top", {"start": v(0.11, 100.25) * mm, "end": v(3.11, 100.25) * mm});
            skLineSegment(sketch, "E218.left", {"start": v(0.11, 91.25) * mm, "end": v(0.11, 100.25) * mm});
            skLineSegment(sketch, "E219", {"start": v(3.11, 100.25) * mm, "end": v(3.11, 94.25) * mm});
            skLineSegment(sketch, "E220", {"start": v(9.61, 94.25) * mm, "end": v(3.11, 94.25) * mm});
            skLineSegment(sketch, "E221", {"start": v(3.11, 91.25) * mm, "end": v(9.61, 91.25) * mm});
            skLineSegment(sketch, "E222.right", {"start": v(15.5, 97.17) * mm, "end": v(15.5, 100.67) * mm});
            skLineSegment(sketch, "E223.bottom", {"start": v(15.5, 97.17) * mm, "end": v(18.5, 97.17) * mm});
            skLineSegment(sketch, "E223.top", {"start": v(15.5, 106.67) * mm, "end": v(18.5, 106.67) * mm});
            skLineSegment(sketch, "E224.bottom", {"start": v(18.5, 106.67) * mm, "end": v(6.5, 106.67) * mm});
            skLineSegment(sketch, "E224.left", {"start": v(18.5, 106.67) * mm, "end": v(18.5, 103.17) * mm});
            skLineSegment(sketch, "E224.right", {"start": v(6.5, 106.67) * mm, "end": v(6.5, 103.17) * mm});
            skLineSegment(sketch, "E225.bottom", {"start": v(6.5, 106.67) * mm, "end": v(9.5, 106.67) * mm});
            skLineSegment(sketch, "E225.top", {"start": v(6.5, 97.17) * mm, "end": v(9.5, 97.17) * mm});
            skLineSegment(sketch, "E225.left", {"start": v(6.5, 106.67) * mm, "end": v(6.5, 97.17) * mm});
            skLineSegment(sketch, "E226.bottom", {"start": v(6.5, 97.17) * mm, "end": v(12.5, 97.17) * mm});
            skLineSegment(sketch, "E226.left", {"start": v(6.5, 97.17) * mm, "end": v(6.5, 100.17) * mm});
            skLineSegment(sketch, "E226.right", {"start": v(12.5, 97.17) * mm, "end": v(12.5, 100.17) * mm});
            skLineSegment(sketch, "E227.right", {"start": v(12.5, 122.17) * mm, "end": v(12.5, 118.67) * mm});
            skLineSegment(sketch, "E228.bottom", {"start": v(12.5, 122.17) * mm, "end": v(15.5, 122.17) * mm});
            skLineSegment(sketch, "E228.top", {"start": v(12.5, 109.67) * mm, "end": v(15.5, 109.67) * mm});
            skPoint(sketch, "E229.oppositeSnap0", {"position": v(0, 117.75) * mm});
            skLineSegment(sketch, "E229.left", {"start": v(15.5, 109.67) * mm, "end": v(15.5, 112.67) * mm});
            skLineSegment(sketch, "E229.right", {"start": v(0, 109.67) * mm, "end": v(0, 112.67) * mm});
            skLineSegment(sketch, "E230.bottom", {"start": v(0, 112.67) * mm, "end": v(3, 112.67) * mm});
            skLineSegment(sketch, "E230.top", {"start": v(0, 103.67) * mm, "end": v(3, 103.67) * mm});
            skLineSegment(sketch, "E231.bottom", {"start": v(3, 103.67) * mm, "end": v(-6.5, 103.67) * mm});
            skLineSegment(sketch, "E231.left", {"start": v(3, 103.67) * mm, "end": v(3, 106.67) * mm});
            skLineSegment(sketch, "E231.right", {"start": v(-6.5, 103.67) * mm, "end": v(-6.5, 106.67) * mm});
            skLineSegment(sketch, "E232", {"start": v(15.5, 112.67) * mm, "end": v(15.5, 118.67) * mm});
            skLineSegment(sketch, "E233", {"start": v(3, 112.67) * mm, "end": v(12.5, 112.67) * mm});
            skLineSegment(sketch, "E234", {"start": v(12.5, 112.67) * mm, "end": v(12.5, 122.17) * mm});
            skLineSegment(sketch, "E235", {"start": v(3, 106.67) * mm, "end": v(3, 109.67) * mm});
            skLineSegment(sketch, "E236", {"start": v(-6.5, 106.67) * mm, "end": v(0, 106.67) * mm});
            skLineSegment(sketch, "E237", {"start": v(0, 106.67) * mm, "end": v(0, 109.67) * mm});
            skLineSegment(sketch, "E238", {"start": v(3, 109.67) * mm, "end": v(12.5, 109.67) * mm});
            skLineSegment(sketch, "E239", {"start": v(18.5, 103.17) * mm, "end": v(18.5, 100.67) * mm});
            skLineSegment(sketch, "E240", {"start": v(9.5, 103.4) * mm, "end": v(15.5, 103.4) * mm});
            skLineSegment(sketch, "E241", {"start": v(15.5, 100.67) * mm, "end": v(15.5, 103.4) * mm});
            skLineSegment(sketch, "E242", {"start": v(9.5, 103.4) * mm, "end": v(9.5, 100.17) * mm});
            skLineSegment(sketch, "E243", {"start": v(9.5, 100.17) * mm, "end": v(12.5, 100.17) * mm});
            skLineSegment(sketch, "E244.right", {"start": v(-22, 122) * mm, "end": v(-22, 119) * mm});
            skLineSegment(sketch, "E245", {"start": v(-22, 119) * mm, "end": v(-12.5, 119) * mm});
            skLineSegment(sketch, "E246", {"start": v(-22, 122) * mm, "end": v(-9.5, 122) * mm});
            skLineSegment(sketch, "E247.right", {"start": v(-22, 100.41) * mm, "end": v(-22, 96.91) * mm});
            skLineSegment(sketch, "E248", {"start": v(-12, 96.91) * mm, "end": v(-22, 96.91) * mm});
            skLineSegment(sketch, "E249", {"start": v(-22, 100.41) * mm, "end": v(-12.04, 100.41) * mm});
            skLineSegment(sketch, "E250.top", {"start": v(-12.4, 88) * mm, "end": v(-9.4, 88) * mm});
            skLineSegment(sketch, "E251", {"start": v(-9.4, 88) * mm, "end": v(-9.4, 91.25) * mm});
            skLineSegment(sketch, "E252", {"start": v(-12.4, 88) * mm, "end": v(-12.4, 91.25) * mm});
            skLineSegment(sketch, "E253.top", {"start": v(9.61, 87.75) * mm, "end": v(12.61, 87.75) * mm});
            skLineSegment(sketch, "E254", {"start": v(9.61, 87.75) * mm, "end": v(9.61, 91.25) * mm});
            skLineSegment(sketch, "E255", {"start": v(12.61, 87.75) * mm, "end": v(12.61, 91.25) * mm});
            skLineSegment(sketch, "E256.right", {"start": v(21.75, 97.17) * mm, "end": v(21.75, 100.67) * mm});
            skLineSegment(sketch, "E257", {"start": v(21.75, 97.17) * mm, "end": v(18.5, 97.17) * mm});
            skLineSegment(sketch, "E258", {"start": v(21.75, 100.67) * mm, "end": v(18.5, 100.67) * mm});
            skLineSegment(sketch, "E259.right", {"start": v(22, 118.67) * mm, "end": v(22, 122.17) * mm});
            skLineSegment(sketch, "E260", {"start": v(22, 118.67) * mm, "end": v(15.5, 118.67) * mm});
            skLineSegment(sketch, "E261", {"start": v(22, 122.17) * mm, "end": v(15.5, 122.17) * mm});
            skLineSegment(sketch, "E262.top", {"start": v(9.5, 131.75) * mm, "end": v(12.5, 131.75) * mm});
            skLineSegment(sketch, "E263", {"start": v(9.5, 131.75) * mm, "end": v(9.5, 128.25) * mm});
            skLineSegment(sketch, "E264", {"start": v(12.5, 131.75) * mm, "end": v(12.5, 128.25) * mm});
            skLineSegment(sketch, "E265.top", {"start": v(-12.5, 131.75) * mm, "end": v(-9.5, 131.75) * mm});
            skLineSegment(sketch, "E266", {"start": v(-12.5, 131.75) * mm, "end": v(-12.5, 128.35) * mm});
            skLineSegment(sketch, "E267", {"start": v(-9.5, 131.75) * mm, "end": v(-9.5, 128.33) * mm});
            skSolve(sketch);
        }
        {
            var Q0;
            Q0=makeQuery(id+"F9.opExtrude","SWEPT_FACE",FACE,{"disambiguationData":[OSD([sQuery(id+"F4.wireOp",EDGE,"E3.right")])]});
            var sketch = newSketch(context, id + "F13", { "sketchPlane" : qUnion([Q0])});
            skLineSegment(sketch, "E268.top", {"start": v(-12.56, 125.35) * mm, "end": v(-9.48, 125.35) * mm});
            skLineSegment(sketch, "E269.left", {"start": v(-12.5, 128.35) * mm, "end": v(-12.5, 125.25) * mm});
            skLineSegment(sketch, "E269.right", {"start": v(-3, 128.33) * mm, "end": v(-3, 125.31) * mm});
            skLineSegment(sketch, "E270.top", {"start": v(-6.5, 116.33) * mm, "end": v(-3, 116.33) * mm});
            skLineSegment(sketch, "E270.left", {"start": v(-6.5, 125.33) * mm, "end": v(-6.5, 116.33) * mm});
            skLineSegment(sketch, "E270.right", {"start": v(-3, 125.31) * mm, "end": v(-3, 116.33) * mm});
            skLineSegment(sketch, "E271", {"start": v(-9.48, 125.35) * mm, "end": v(-6.5, 125.33) * mm});
            skLineSegment(sketch, "E272", {"start": v(-3, 128.33) * mm, "end": v(-9.5, 128.33) * mm});
            skLineSegment(sketch, "E273.top", {"start": v(9.5, 125.25) * mm, "end": v(12.5, 125.25) * mm});
            skLineSegment(sketch, "E274.left", {"start": v(12.5, 125.25) * mm, "end": v(12.5, 128.25) * mm});
            skLineSegment(sketch, "E274.right", {"start": v(0, 125.25) * mm, "end": v(0, 128.25) * mm});
            skLineSegment(sketch, "E275.bottom", {"start": v(0, 128.25) * mm, "end": v(3, 128.25) * mm});
            skLineSegment(sketch, "E275.top", {"start": v(0, 116.25) * mm, "end": v(3, 116.25) * mm});
            skLineSegment(sketch, "E275.left", {"start": v(0, 128.25) * mm, "end": v(0, 116.25) * mm});
            skLineSegment(sketch, "E276.bottom", {"start": v(0, 116.25) * mm, "end": v(9, 116.25) * mm});
            skLineSegment(sketch, "E276.left", {"start": v(0, 116.25) * mm, "end": v(0, 119.25) * mm});
            skLineSegment(sketch, "E276.right", {"start": v(9, 116.25) * mm, "end": v(9, 119.25) * mm});
            skLineSegment(sketch, "E277.bottom", {"start": v(9, 116.25) * mm, "end": v(6.5, 116.25) * mm});
            skLineSegment(sketch, "E277.top", {"start": v(9, 121.75) * mm, "end": v(6.5, 121.75) * mm});
            skLineSegment(sketch, "E277.left", {"start": v(9, 116.25) * mm, "end": v(9, 121.75) * mm});
            skLineSegment(sketch, "E278", {"start": v(6.5, 121.75) * mm, "end": v(6.5, 119.25) * mm});
            skLineSegment(sketch, "E279", {"start": v(3, 125.25) * mm, "end": v(3, 119.25) * mm});
            skLineSegment(sketch, "E280", {"start": v(3, 119.25) * mm, "end": v(6.5, 119.25) * mm});
            skLineSegment(sketch, "E281", {"start": v(3, 128.25) * mm, "end": v(9.5, 128.25) * mm});
            skLineSegment(sketch, "E282", {"start": v(3, 125.25) * mm, "end": v(9.5, 125.25) * mm});
            skLineSegment(sketch, "E283.right", {"start": v(-9.5, 122) * mm, "end": v(-9.5, 119) * mm});
            skLineSegment(sketch, "E284.top", {"start": v(-9.5, 110) * mm, "end": v(-12.5, 110) * mm});
            skLineSegment(sketch, "E284.right", {"start": v(-12.5, 119) * mm, "end": v(-12.5, 110) * mm});
            skLineSegment(sketch, "E285.bottom", {"start": v(-12.5, 110) * mm, "end": v(-3, 110) * mm});
            skLineSegment(sketch, "E285.left", {"start": v(-12.5, 110) * mm, "end": v(-12.5, 112.5) * mm});
            skLineSegment(sketch, "E285.right", {"start": v(-3, 110) * mm, "end": v(-3, 112.5) * mm});
            skLineSegment(sketch, "E286", {"start": v(-9.5, 119) * mm, "end": v(-9.5, 112.5) * mm});
            skLineSegment(sketch, "E287", {"start": v(-9.5, 112.5) * mm, "end": v(-3, 112.5) * mm});
            skLineSegment(sketch, "E288.right", {"start": v(-9.5, 100.41) * mm, "end": v(-9.5, 96.91) * mm});
            skLineSegment(sketch, "E289.bottom", {"start": v(-9.5, 96.91) * mm, "end": v(-12, 96.91) * mm});
            skLineSegment(sketch, "E289.top", {"start": v(-9.5, 106.91) * mm, "end": v(-12.04, 106.91) * mm});
            skLineSegment(sketch, "E289.left", {"start": v(-9.5, 96.91) * mm, "end": v(-9.5, 106.91) * mm});
            skLineSegment(sketch, "E290.left", {"start": v(-9.5, 106.91) * mm, "end": v(-9.5, 103.41) * mm});
            skLineSegment(sketch, "E290.right", {"start": v(-18.5, 106.91) * mm, "end": v(-18.5, 103.41) * mm});
            skLineSegment(sketch, "E291.bottom", {"start": v(-18.5, 103.41) * mm, "end": v(-15.5, 103.41) * mm});
            skLineSegment(sketch, "E291.top", {"start": v(-18.5, 115.91) * mm, "end": v(-15.54, 115.91) * mm});
            skLineSegment(sketch, "E291.left", {"start": v(-18.5, 103.41) * mm, "end": v(-18.5, 115.91) * mm});
            skLineSegment(sketch, "E292", {"start": v(-12.04, 100.41) * mm, "end": v(-12.04, 103.41) * mm});
            skLineSegment(sketch, "E293", {"start": v(-15.54, 115.91) * mm, "end": v(-15.54, 106.91) * mm});
            skLineSegment(sketch, "E294", {"start": v(-12.04, 106.91) * mm, "end": v(-15.54, 106.91) * mm});
            skLineSegment(sketch, "E295", {"start": v(-12.04, 103.41) * mm, "end": v(-15.5, 103.41) * mm});
            skLineSegment(sketch, "E296.top", {"start": v(-12.4, 94.25) * mm, "end": v(-9.44, 94.25) * mm});
            skLineSegment(sketch, "E297.left", {"start": v(-12.4, 94.25) * mm, "end": v(-12.4, 91.25) * mm});
            skLineSegment(sketch, "E297.right", {"start": v(-2.94, 94.25) * mm, "end": v(-2.94, 91.25) * mm});
            skLineSegment(sketch, "E298.bottom", {"start": v(-2.94, 91.25) * mm, "end": v(-6.4, 91.25) * mm});
            skLineSegment(sketch, "E298.top", {"start": v(-2.94, 100.75) * mm, "end": v(-6.44, 100.75) * mm});
            skLineSegment(sketch, "E298.left", {"start": v(-2.94, 91.25) * mm, "end": v(-2.94, 100.75) * mm});
            skLineSegment(sketch, "E299", {"start": v(-6.4, 91.25) * mm, "end": v(-9.4, 91.25) * mm});
            skLineSegment(sketch, "E300", {"start": v(-6.44, 100.75) * mm, "end": v(-6.44, 94.25) * mm});
            skLineSegment(sketch, "E301", {"start": v(-9.44, 94.25) * mm, "end": v(-6.44, 94.25) * mm});
            skLineSegment(sketch, "E302.top", {"start": v(12.61, 94.25) * mm, "end": v(9.61, 94.25) * mm});
            skLineSegment(sketch, "E303.left", {"start": v(12.61, 94.25) * mm, "end": v(12.61, 91.25) * mm});
            skLineSegment(sketch, "E303.right", {"start": v(0.11, 94.25) * mm, "end": v(0.11, 91.25) * mm});
            skLineSegment(sketch, "E304.bottom", {"start": v(0.11, 91.25) * mm, "end": v(3.11, 91.25) * mm});
            skLineSegment(sketch, "E304.top", {"start": v(0.11, 100.25) * mm, "end": v(3.11, 100.25) * mm});
            skLineSegment(sketch, "E304.left", {"start": v(0.11, 91.25) * mm, "end": v(0.11, 100.25) * mm});
            skLineSegment(sketch, "E305", {"start": v(3.11, 100.25) * mm, "end": v(3.11, 94.25) * mm});
            skLineSegment(sketch, "E306", {"start": v(9.61, 94.25) * mm, "end": v(3.11, 94.25) * mm});
            skLineSegment(sketch, "E307", {"start": v(3.11, 91.25) * mm, "end": v(9.61, 91.25) * mm});
            skLineSegment(sketch, "E308.right", {"start": v(15.5, 97.17) * mm, "end": v(15.5, 100.67) * mm});
            skLineSegment(sketch, "E309.bottom", {"start": v(15.5, 97.17) * mm, "end": v(18.5, 97.17) * mm});
            skLineSegment(sketch, "E309.top", {"start": v(15.5, 106.67) * mm, "end": v(18.5, 106.67) * mm});
            skLineSegment(sketch, "E310.bottom", {"start": v(18.5, 106.67) * mm, "end": v(6.5, 106.67) * mm});
            skLineSegment(sketch, "E310.left", {"start": v(18.5, 106.67) * mm, "end": v(18.5, 103.17) * mm});
            skLineSegment(sketch, "E310.right", {"start": v(6.5, 106.67) * mm, "end": v(6.5, 103.17) * mm});
            skLineSegment(sketch, "E311.bottom", {"start": v(6.5, 106.67) * mm, "end": v(9.5, 106.67) * mm});
            skLineSegment(sketch, "E311.top", {"start": v(6.5, 97.17) * mm, "end": v(9.5, 97.17) * mm});
            skLineSegment(sketch, "E311.left", {"start": v(6.5, 106.67) * mm, "end": v(6.5, 97.17) * mm});
            skLineSegment(sketch, "E312.bottom", {"start": v(6.5, 97.17) * mm, "end": v(12.5, 97.17) * mm});
            skLineSegment(sketch, "E312.left", {"start": v(6.5, 97.17) * mm, "end": v(6.5, 100.17) * mm});
            skLineSegment(sketch, "E312.right", {"start": v(12.5, 97.17) * mm, "end": v(12.5, 100.17) * mm});
            skLineSegment(sketch, "E313.right", {"start": v(12.5, 122.17) * mm, "end": v(12.5, 118.67) * mm});
            skLineSegment(sketch, "E314.bottom", {"start": v(12.5, 122.17) * mm, "end": v(15.5, 122.17) * mm});
            skLineSegment(sketch, "E314.top", {"start": v(12.5, 109.67) * mm, "end": v(15.5, 109.67) * mm});
            skPoint(sketch, "E315.oppositeSnap0", {"position": v(0, 117.75) * mm});
            skLineSegment(sketch, "E315.left", {"start": v(15.5, 109.67) * mm, "end": v(15.5, 112.67) * mm});
            skLineSegment(sketch, "E315.right", {"start": v(0, 109.67) * mm, "end": v(0, 112.67) * mm});
            skLineSegment(sketch, "E316.bottom", {"start": v(0, 112.67) * mm, "end": v(3, 112.67) * mm});
            skLineSegment(sketch, "E316.top", {"start": v(0, 103.67) * mm, "end": v(3, 103.67) * mm});
            skLineSegment(sketch, "E317.bottom", {"start": v(3, 103.67) * mm, "end": v(-6.5, 103.67) * mm});
            skLineSegment(sketch, "E317.left", {"start": v(3, 103.67) * mm, "end": v(3, 106.67) * mm});
            skLineSegment(sketch, "E317.right", {"start": v(-6.5, 103.67) * mm, "end": v(-6.5, 106.67) * mm});
            skLineSegment(sketch, "E318", {"start": v(15.5, 112.67) * mm, "end": v(15.5, 118.67) * mm});
            skLineSegment(sketch, "E319", {"start": v(3, 112.67) * mm, "end": v(12.5, 112.67) * mm});
            skLineSegment(sketch, "E320", {"start": v(12.5, 112.67) * mm, "end": v(12.5, 122.17) * mm});
            skLineSegment(sketch, "E321", {"start": v(3, 106.67) * mm, "end": v(3, 109.67) * mm});
            skLineSegment(sketch, "E322", {"start": v(-6.5, 106.67) * mm, "end": v(0, 106.67) * mm});
            skLineSegment(sketch, "E323", {"start": v(0, 106.67) * mm, "end": v(0, 109.67) * mm});
            skLineSegment(sketch, "E324", {"start": v(3, 109.67) * mm, "end": v(12.5, 109.67) * mm});
            skLineSegment(sketch, "E325", {"start": v(18.5, 103.17) * mm, "end": v(18.5, 100.67) * mm});
            skLineSegment(sketch, "E326", {"start": v(9.5, 103.4) * mm, "end": v(15.5, 103.4) * mm});
            skLineSegment(sketch, "E327", {"start": v(15.5, 100.67) * mm, "end": v(15.5, 103.4) * mm});
            skLineSegment(sketch, "E328", {"start": v(9.5, 103.4) * mm, "end": v(9.5, 100.17) * mm});
            skLineSegment(sketch, "E329", {"start": v(9.5, 100.17) * mm, "end": v(12.5, 100.17) * mm});
            skLineSegment(sketch, "E330.right", {"start": v(-22, 122) * mm, "end": v(-22, 119) * mm});
            skLineSegment(sketch, "E331", {"start": v(-22, 119) * mm, "end": v(-12.5, 119) * mm});
            skLineSegment(sketch, "E332", {"start": v(-22, 122) * mm, "end": v(-9.5, 122) * mm});
            skLineSegment(sketch, "E333.right", {"start": v(-22, 100.41) * mm, "end": v(-22, 96.91) * mm});
            skLineSegment(sketch, "E334", {"start": v(-12, 96.91) * mm, "end": v(-22, 96.91) * mm});
            skLineSegment(sketch, "E335", {"start": v(-22, 100.41) * mm, "end": v(-12.04, 100.41) * mm});
            skLineSegment(sketch, "E336.top", {"start": v(-12.4, 88) * mm, "end": v(-9.4, 88) * mm});
            skLineSegment(sketch, "E337", {"start": v(-9.4, 88) * mm, "end": v(-9.4, 91.25) * mm});
            skLineSegment(sketch, "E338", {"start": v(-12.4, 88) * mm, "end": v(-12.4, 91.25) * mm});
            skLineSegment(sketch, "E339.top", {"start": v(9.61, 87.75) * mm, "end": v(12.61, 87.75) * mm});
            skLineSegment(sketch, "E340", {"start": v(9.61, 87.75) * mm, "end": v(9.61, 91.25) * mm});
            skLineSegment(sketch, "E341", {"start": v(12.61, 87.75) * mm, "end": v(12.61, 91.25) * mm});
            skLineSegment(sketch, "E342.right", {"start": v(21.75, 97.17) * mm, "end": v(21.75, 100.67) * mm});
            skLineSegment(sketch, "E343", {"start": v(21.75, 97.17) * mm, "end": v(18.5, 97.17) * mm});
            skLineSegment(sketch, "E344", {"start": v(21.75, 100.67) * mm, "end": v(18.5, 100.67) * mm});
            skLineSegment(sketch, "E345.right", {"start": v(22, 118.67) * mm, "end": v(22, 122.17) * mm});
            skLineSegment(sketch, "E346", {"start": v(22, 118.67) * mm, "end": v(15.5, 118.67) * mm});
            skLineSegment(sketch, "E347", {"start": v(22, 122.17) * mm, "end": v(15.5, 122.17) * mm});
            skLineSegment(sketch, "E348.top", {"start": v(9.5, 131.75) * mm, "end": v(12.5, 131.75) * mm});
            skLineSegment(sketch, "E349", {"start": v(9.5, 131.75) * mm, "end": v(9.5, 128.25) * mm});
            skLineSegment(sketch, "E350", {"start": v(12.5, 131.75) * mm, "end": v(12.5, 128.25) * mm});
            skLineSegment(sketch, "E351.top", {"start": v(-12.5, 131.75) * mm, "end": v(-9.5, 131.75) * mm});
            skLineSegment(sketch, "E352", {"start": v(-12.5, 131.75) * mm, "end": v(-12.5, 128.35) * mm});
            skLineSegment(sketch, "E353", {"start": v(-9.5, 131.75) * mm, "end": v(-9.5, 128.33) * mm});
            skSolve(sketch);
        }
        {
            var Q0;
            Q0 = qSketchRegion(id + "F10", true);
            extrude(context, id + "F14", {"entities" : qUnion([Q0]), "operationType" : NewBodyOperationType.REMOVE, "oppositeDirection" : true, "depth" : 5 * mm});
        }
        {
            var Q0;
            Q0 = qSketchRegion(id + "F11", true);
            extrude(context, id + "F15", {"entities" : qUnion([Q0]), "operationType" : NewBodyOperationType.REMOVE, "oppositeDirection" : true, "depth" : 5 * mm});
        }
        {
            var Q0;
            Q0 = qSketchRegion(id + "F12", true);
            extrude(context, id + "F16", {"entities" : qUnion([Q0]), "operationType" : NewBodyOperationType.REMOVE, "oppositeDirection" : true, "depth" : 5 * mm});
        }
        {
            var Q0;
            Q0 = qSketchRegion(id + "F13", true);
            extrude(context, id + "F17", {"entities" : qUnion([Q0]), "operationType" : NewBodyOperationType.REMOVE, "oppositeDirection" : true, "depth" : 5 * mm});
        }
        {
            var Q0;
            Q0=makeQuery(id+"F1.opExtrude","CAP_FACE",FACE,{"disambiguationData":[OSD([sQuery(id+"F0.wireOp",EDGE,"E0")])],"isStart":false});
            var sketch = newSketch(context, id + "F18", { "sketchPlane" : qUnion([Q0])});
            skCircle(sketch, "E354", {"center": v(0, 0) * mm, "radius": 12.5 * mm});
            skSolve(sketch);
        }
        {
            var Q0;
            Q0 = qSketchRegion(id + "F18", true);
            extrude(context, id + "F19", {"entities" : qUnion([Q0]), "operationType" : NewBodyOperationType.REMOVE, "oppositeDirection" : true, "depth" : 5 * mm});
        }
        {
            var Q0;
            Q0=makeQuery(id+"F1.opExtrude","CAP_FACE",FACE,{"disambiguationData":[OSD([sQuery(id+"F0.wireOp",EDGE,"E0")])],"isStart":true});
            var sketch = newSketch(context, id + "F20", { "sketchPlane" : qUnion([Q0])});
            skCircle(sketch, "E355", {"center": v(0, 0) * mm, "radius": 35 * mm});
            skSolve(sketch);
        }
        {
            var Q0;
            Q0 = qSketchRegion(id + "F20", true);
            extrude(context, id + "F21", {"entities" : qUnion([Q0]), "operationType" : NewBodyOperationType.REMOVE, "oppositeDirection" : true, "depth" : 10 * mm});
        }
    });
